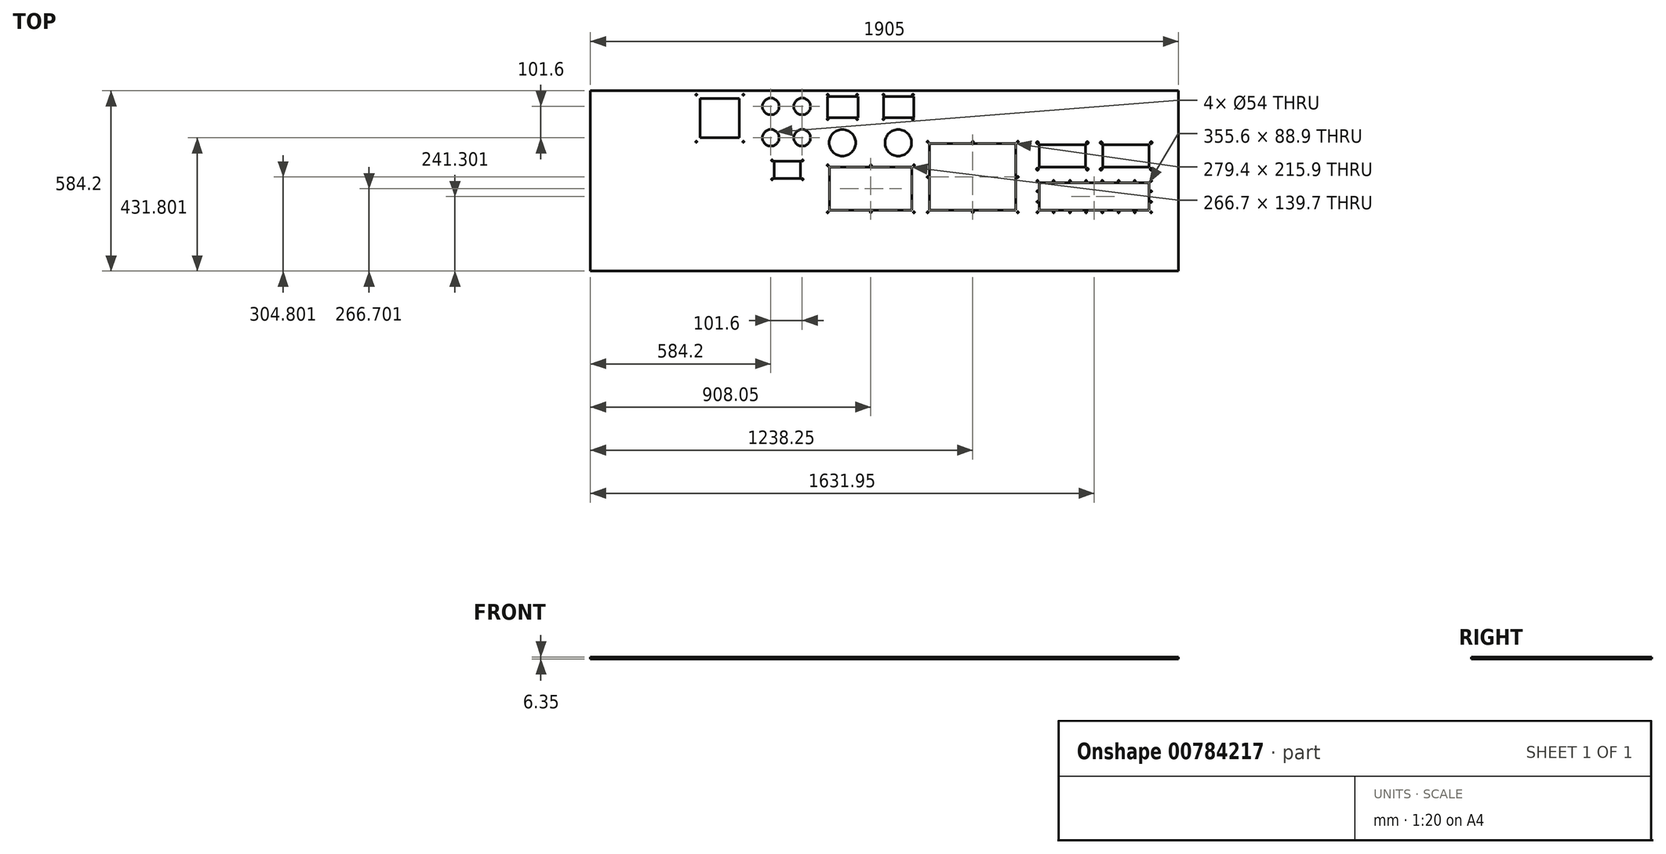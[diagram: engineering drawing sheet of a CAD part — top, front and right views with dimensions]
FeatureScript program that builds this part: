
annotation { "Feature Type Name" : "Feature", "Feature Type Description" : "" }
export const myFeature = defineFeature(function(context is Context, id is Id, definition is map)
    precondition{}
    {
        {
            var Q0;
            Q0=qCreatedBy(makeId("Top.planeOp"),FACE);
            var sketch = newSketch(context, id + "F0", { "sketchPlane" : qUnion([Q0])});
            skLineSegment(sketch, "E0.bottom", {"start": v(-452.65, 333.51) * mm, "end": v(1452.35, 333.51) * mm});
            skLineSegment(sketch, "E0.top", {"start": v(-452.65, -250.69) * mm, "end": v(1452.35, -250.69) * mm});
            skLineSegment(sketch, "E0.left", {"start": v(-452.65, 333.51) * mm, "end": v(-452.65, -250.69) * mm});
            skLineSegment(sketch, "E0.right", {"start": v(1452.35, 333.51) * mm, "end": v(1452.35, -250.69) * mm});
            skPoint(sketch, "E1", {"position": v(995.15, 41.41) * mm});
            skPoint(sketch, "E2", {"position": v(1363.45, 41.41) * mm});
            skPoint(sketch, "E3", {"position": v(1363.45, -60.19) * mm});
            skPoint(sketch, "E4", {"position": v(995.15, -60.19) * mm});
            skLineSegment(sketch, "E5", {"start": v(995.15, 41.41) * mm, "end": v(995.15, -60.19) * mm});
            skPoint(sketch, "E6", {"position": v(995.15, 7.63) * mm});
            skPoint(sketch, "E7", {"position": v(995.15, -26.15) * mm});
            skLineSegment(sketch, "E8", {"start": v(995.15, 41.41) * mm, "end": v(1363.45, 41.41) * mm});
            skLineSegment(sketch, "E9", {"start": v(1363.45, 41.41) * mm, "end": v(1363.45, -60.19) * mm});
            skLineSegment(sketch, "E10", {"start": v(1363.45, -60.19) * mm, "end": v(995.15, -60.19) * mm});
            skPoint(sketch, "E11", {"position": v(1047.73, 41.41) * mm});
            skPoint(sketch, "E12", {"position": v(1100.3, 41.41) * mm});
            skPoint(sketch, "E13", {"position": v(1152.88, 41.41) * mm});
            skPoint(sketch, "E14", {"position": v(1205.46, 41.41) * mm});
            skPoint(sketch, "E15", {"position": v(1258.04, 41.41) * mm});
            skPoint(sketch, "E16", {"position": v(1310.62, 41.41) * mm});
            skPoint(sketch, "E17", {"position": v(1047.73, -60.19) * mm});
            skPoint(sketch, "E18", {"position": v(1100.3, -60.19) * mm});
            skPoint(sketch, "E19", {"position": v(1152.88, -60.19) * mm});
            skPoint(sketch, "E20", {"position": v(1205.46, -60.19) * mm});
            skPoint(sketch, "E21", {"position": v(1258.04, -60.19) * mm});
            skPoint(sketch, "E22", {"position": v(1310.62, -60.19) * mm});
            skPoint(sketch, "E23", {"position": v(1363.45, 7.63) * mm});
            skPoint(sketch, "E24", {"position": v(1363.45, -26.4) * mm});
            skLineSegment(sketch, "E25.bottom", {"start": v(1001.5, 35.06) * mm, "end": v(1357.1, 35.06) * mm});
            skLineSegment(sketch, "E25.top", {"start": v(1001.5, -53.84) * mm, "end": v(1357.1, -53.84) * mm});
            skLineSegment(sketch, "E25.left", {"start": v(1001.5, 35.06) * mm, "end": v(1001.5, -53.84) * mm});
            skLineSegment(sketch, "E25.right", {"start": v(1357.1, 35.06) * mm, "end": v(1357.1, -53.84) * mm});
            skPoint(sketch, "E26", {"position": v(639.55, 168.41) * mm});
            skPoint(sketch, "E27", {"position": v(931.65, 168.41) * mm});
            skPoint(sketch, "E28", {"position": v(931.65, -60.19) * mm});
            skPoint(sketch, "E29", {"position": v(639.55, -60.19) * mm});
            skPoint(sketch, "E30", {"position": v(785.6, 168.41) * mm});
            skPoint(sketch, "E31", {"position": v(785.6, -60.19) * mm});
            skPoint(sketch, "E32", {"position": v(639.55, 54.11) * mm});
            skPoint(sketch, "E33", {"position": v(931.65, 54.11) * mm});
            skLineSegment(sketch, "E34", {"start": v(639.55, 168.41) * mm, "end": v(639.55, 54.11) * mm});
            skLineSegment(sketch, "E35", {"start": v(639.55, -60.19) * mm, "end": v(639.55, 54.11) * mm});
            skLineSegment(sketch, "E36", {"start": v(639.55, -60.19) * mm, "end": v(785.6, -60.19) * mm});
            skLineSegment(sketch, "E37", {"start": v(931.65, -60.19) * mm, "end": v(785.6, -60.19) * mm});
            skLineSegment(sketch, "E38", {"start": v(931.65, -60.19) * mm, "end": v(931.65, 168.41) * mm});
            skLineSegment(sketch, "E39", {"start": v(931.65, 168.41) * mm, "end": v(639.55, 168.41) * mm});
            skLineSegment(sketch, "E40.bottom", {"start": v(645.9, 162.06) * mm, "end": v(925.3, 162.06) * mm});
            skLineSegment(sketch, "E40.top", {"start": v(645.9, -53.84) * mm, "end": v(925.3, -53.84) * mm});
            skLineSegment(sketch, "E40.left", {"start": v(645.9, 162.06) * mm, "end": v(645.9, -53.84) * mm});
            skLineSegment(sketch, "E40.right", {"start": v(925.3, 162.06) * mm, "end": v(925.3, -53.84) * mm});
            skPoint(sketch, "E41", {"position": v(315.7, 92.21) * mm});
            skPoint(sketch, "E42", {"position": v(315.7, -60.19) * mm});
            skPoint(sketch, "E43", {"position": v(595.1, -60.19) * mm});
            skPoint(sketch, "E44", {"position": v(595.1, 92.21) * mm});
            skPoint(sketch, "E45", {"position": v(455.4, 92.21) * mm});
            skPoint(sketch, "E46", {"position": v(455.4, -60.19) * mm});
            skLineSegment(sketch, "E47", {"start": v(315.7, 92.21) * mm, "end": v(595.1, 92.21) * mm});
            skLineSegment(sketch, "E48", {"start": v(595.1, -60.19) * mm, "end": v(595.1, 92.21) * mm});
            skLineSegment(sketch, "E49", {"start": v(595.1, -60.19) * mm, "end": v(315.7, -60.19) * mm});
            skLineSegment(sketch, "E50", {"start": v(315.7, -60.19) * mm, "end": v(315.7, 92.21) * mm});
            skLineSegment(sketch, "E51.bottom", {"start": v(322.05, 85.86) * mm, "end": v(588.75, 85.86) * mm});
            skLineSegment(sketch, "E51.top", {"start": v(322.05, -53.84) * mm, "end": v(588.75, -53.84) * mm});
            skLineSegment(sketch, "E51.left", {"start": v(322.05, 85.86) * mm, "end": v(322.05, -53.84) * mm});
            skLineSegment(sketch, "E51.right", {"start": v(588.75, 85.86) * mm, "end": v(588.75, -53.84) * mm});
            skPoint(sketch, "E52", {"position": v(995.15, 165.11) * mm});
            skPoint(sketch, "E53", {"position": v(995.15, 79.51) * mm});
            skPoint(sketch, "E54", {"position": v(1156.95, 79.51) * mm});
            skPoint(sketch, "E55", {"position": v(1156.95, 165.11) * mm});
            skLineSegment(sketch, "E56", {"start": v(995.15, 165.11) * mm, "end": v(995.15, 79.51) * mm});
            skLineSegment(sketch, "E57", {"start": v(995.15, 79.51) * mm, "end": v(1156.95, 79.51) * mm});
            skLineSegment(sketch, "E58", {"start": v(1156.95, 79.51) * mm, "end": v(1156.95, 165.11) * mm});
            skLineSegment(sketch, "E59", {"start": v(1156.95, 165.11) * mm, "end": v(995.15, 165.11) * mm});
            skLineSegment(sketch, "E60.bottom", {"start": v(1001.5, 158.76) * mm, "end": v(1150.6, 158.76) * mm});
            skLineSegment(sketch, "E60.top", {"start": v(1001.5, 85.86) * mm, "end": v(1150.6, 85.86) * mm});
            skLineSegment(sketch, "E60.left", {"start": v(1001.5, 158.76) * mm, "end": v(1001.5, 85.86) * mm});
            skLineSegment(sketch, "E60.right", {"start": v(1150.6, 158.76) * mm, "end": v(1150.6, 85.86) * mm});
            skPoint(sketch, "E61", {"position": v(1201.65, 165.11) * mm});
            skPoint(sketch, "E62", {"position": v(1201.65, 79.51) * mm});
            skPoint(sketch, "E63", {"position": v(1363.45, 79.51) * mm});
            skPoint(sketch, "E64", {"position": v(1363.45, 165.11) * mm});
            skLineSegment(sketch, "E65", {"start": v(1201.65, 165.11) * mm, "end": v(1201.65, 79.51) * mm});
            skLineSegment(sketch, "E66", {"start": v(1201.65, 79.51) * mm, "end": v(1363.45, 79.51) * mm});
            skLineSegment(sketch, "E67", {"start": v(1363.45, 79.51) * mm, "end": v(1363.45, 165.11) * mm});
            skLineSegment(sketch, "E68", {"start": v(1363.45, 165.11) * mm, "end": v(1201.65, 165.11) * mm});
            skLineSegment(sketch, "E69.bottom", {"start": v(1206.48, 158.76) * mm, "end": v(1357.1, 158.76) * mm});
            skLineSegment(sketch, "E69.top", {"start": v(1206.48, 85.86) * mm, "end": v(1357.1, 85.86) * mm});
            skLineSegment(sketch, "E69.left", {"start": v(1206.48, 158.76) * mm, "end": v(1206.48, 85.86) * mm});
            skLineSegment(sketch, "E69.right", {"start": v(1357.1, 158.76) * mm, "end": v(1357.1, 85.86) * mm});
            skPoint(sketch, "E70", {"position": v(315.7, 320.81) * mm});
            skPoint(sketch, "E71", {"position": v(315.7, 241.34) * mm});
            skPoint(sketch, "E72", {"position": v(411.18, 241.34) * mm});
            skPoint(sketch, "E73", {"position": v(411.18, 320.81) * mm});
            skLineSegment(sketch, "E74", {"start": v(315.7, 320.81) * mm, "end": v(411.18, 320.81) * mm});
            skLineSegment(sketch, "E75", {"start": v(411.18, 241.34) * mm, "end": v(411.18, 320.81) * mm});
            skLineSegment(sketch, "E76", {"start": v(411.18, 241.34) * mm, "end": v(315.7, 241.34) * mm});
            skLineSegment(sketch, "E77", {"start": v(315.7, 241.34) * mm, "end": v(315.7, 320.81) * mm});
            skLineSegment(sketch, "E78.bottom", {"start": v(315.7, 314.46) * mm, "end": v(414.13, 314.46) * mm});
            skLineSegment(sketch, "E78.top", {"start": v(315.7, 246.2) * mm, "end": v(414.13, 246.2) * mm});
            skLineSegment(sketch, "E78.left", {"start": v(315.7, 314.46) * mm, "end": v(315.7, 246.2) * mm});
            skLineSegment(sketch, "E78.right", {"start": v(414.13, 314.46) * mm, "end": v(414.13, 246.2) * mm});
            skPoint(sketch, "E79", {"position": v(496.68, 320.81) * mm});
            skPoint(sketch, "E80", {"position": v(496.68, 241.34) * mm});
            skPoint(sketch, "E81", {"position": v(592.15, 241.34) * mm});
            skPoint(sketch, "E82", {"position": v(592.15, 320.81) * mm});
            skLineSegment(sketch, "E83", {"start": v(496.68, 320.81) * mm, "end": v(592.15, 320.81) * mm});
            skLineSegment(sketch, "E84", {"start": v(592.15, 241.34) * mm, "end": v(592.15, 320.81) * mm});
            skLineSegment(sketch, "E85", {"start": v(592.15, 241.34) * mm, "end": v(496.68, 241.34) * mm});
            skLineSegment(sketch, "E86", {"start": v(496.68, 241.34) * mm, "end": v(496.68, 320.81) * mm});
            skLineSegment(sketch, "E87.bottom", {"start": v(496.68, 314.46) * mm, "end": v(595.1, 314.46) * mm});
            skLineSegment(sketch, "E87.top", {"start": v(496.68, 246.2) * mm, "end": v(595.1, 246.2) * mm});
            skLineSegment(sketch, "E87.left", {"start": v(496.68, 314.46) * mm, "end": v(496.68, 246.2) * mm});
            skLineSegment(sketch, "E87.right", {"start": v(595.1, 314.46) * mm, "end": v(595.1, 246.2) * mm});
            skPoint(sketch, "E88", {"position": v(233.15, 282.71) * mm});
            skPoint(sketch, "E89", {"position": v(233.15, 181.11) * mm});
            skPoint(sketch, "E90", {"position": v(131.55, 282.71) * mm});
            skPoint(sketch, "E91", {"position": v(131.55, 181.11) * mm});
            skPoint(sketch, "E92", {"position": v(363.44, 165.14) * mm});
            skPoint(sketch, "E92.positionSnap0", {"position": v(363.44, 241.34) * mm});
            skPoint(sketch, "E93", {"position": v(544.41, 165.14) * mm});
            skPoint(sketch, "E93.positionSnap0", {"position": v(544.41, 241.34) * mm});
            skPoint(sketch, "E94", {"position": v(135.61, 107.93) * mm});
            skPoint(sketch, "E95", {"position": v(234.61, 107.93) * mm});
            skPoint(sketch, "E96", {"position": v(234.61, 46.72) * mm});
            skPoint(sketch, "E97", {"position": v(135.61, 46.72) * mm});
            skLineSegment(sketch, "E98.bottom", {"start": v(143.03, 104.91) * mm, "end": v(227.2, 104.91) * mm});
            skLineSegment(sketch, "E98.top", {"start": v(143.03, 49.75) * mm, "end": v(227.2, 49.75) * mm});
            skLineSegment(sketch, "E98.left", {"start": v(143.03, 104.91) * mm, "end": v(143.03, 49.75) * mm});
            skLineSegment(sketch, "E98.right", {"start": v(227.2, 104.91) * mm, "end": v(227.2, 49.75) * mm});
            skLineSegment(sketch, "E99", {"start": v(131.55, 181.11) * mm, "end": v(233.15, 181.11) * mm});
            skPoint(sketch, "E100", {"position": v(-109.75, 320.81) * mm});
            skPoint(sketch, "E101", {"position": v(42.65, 320.81) * mm});
            skPoint(sketch, "E102", {"position": v(42.65, 168.41) * mm});
            skPoint(sketch, "E103", {"position": v(-109.75, 168.41) * mm});
            skLineSegment(sketch, "E104.bottom", {"start": v(-97.05, 308.11) * mm, "end": v(29.95, 308.11) * mm});
            skLineSegment(sketch, "E104.top", {"start": v(-97.05, 181.11) * mm, "end": v(29.95, 181.11) * mm});
            skLineSegment(sketch, "E104.left", {"start": v(-97.05, 308.11) * mm, "end": v(-97.05, 181.11) * mm});
            skLineSegment(sketch, "E104.right", {"start": v(29.95, 308.11) * mm, "end": v(29.95, 181.11) * mm});
            skSolve(sketch);
        }
        {
            var Q0;
            Q0=makeQuery(id+"F0.imprint","IMPRINT",FACE,{"disambiguationData":[TD([[makeQuery(id+"F0.imprint","IMPRINT",EDGE,{"derivedFrom":sQuery(id+"F0.wireOp",EDGE,"E0.bottom")}),-1.0]])]});
            var Q1;
            Q1=makeQuery(id+"F0.imprint","IMPRINT",FACE,{"disambiguationData":[TD([[makeQuery(id+"F0.imprint","IMPRINT",EDGE,{"derivedFrom":sQuery(id+"F0.wireOp",EDGE,"E5")}),1.0]])]});
            var Q2;
            Q2=makeQuery(id+"F0.imprint","IMPRINT",FACE,{"disambiguationData":[TD([[makeQuery(id+"F0.imprint","IMPRINT",EDGE,{"derivedFrom":sQuery(id+"F0.wireOp",EDGE,"E34")}),1.0]])]});
            var Q3;
            Q3=makeQuery(id+"F0.imprint","IMPRINT",FACE,{"disambiguationData":[TD([[makeQuery(id+"F0.imprint","IMPRINT",EDGE,{"derivedFrom":sQuery(id+"F0.wireOp",EDGE,"E47")}),-1.0]])]});
            var Q4;
            Q4=makeQuery(id+"F0.imprint","IMPRINT",FACE,{"disambiguationData":[TD([[makeQuery(id+"F0.imprint","IMPRINT",EDGE,{"derivedFrom":sQuery(id+"F0.wireOp",EDGE,"E56")}),1.0]])]});
            var Q5;
            Q5=makeQuery(id+"F0.imprint","IMPRINT",FACE,{"disambiguationData":[TD([[makeQuery(id+"F0.imprint","IMPRINT",EDGE,{"derivedFrom":sQuery(id+"F0.wireOp",EDGE,"E65")}),1.0]])]});
            var Q6;
            {var subQ0=sQuery(id+"F0.wireOp",EDGE,"E74");Q6=makeQuery(id+"F0.imprint","IMPRINT",FACE,{"disambiguationData":[TD([[makeQuery(id+"F0.imprint","IMPRINT",EDGE,{"derivedFrom":subQ0}),-1.0]])]});}
            var Q7;
            {var subQ0=sQuery(id+"F0.wireOp",EDGE,"E76");Q7=makeQuery(id+"F0.imprint","IMPRINT",FACE,{"disambiguationData":[TD([[makeQuery(id+"F0.imprint","IMPRINT",EDGE,{"derivedFrom":subQ0}),-1.0]])]});}
            var Q8;
            {var subQ0=sQuery(id+"F0.wireOp",EDGE,"E83");Q8=makeQuery(id+"F0.imprint","IMPRINT",FACE,{"disambiguationData":[TD([[makeQuery(id+"F0.imprint","IMPRINT",EDGE,{"derivedFrom":subQ0}),-1.0]])]});}
            var Q9;
            {var subQ0=sQuery(id+"F0.wireOp",EDGE,"E85");Q9=makeQuery(id+"F0.imprint","IMPRINT",FACE,{"disambiguationData":[TD([[makeQuery(id+"F0.imprint","IMPRINT",EDGE,{"derivedFrom":subQ0}),-1.0]])]});}
            extrude(context, id + "F1", {"entities" : qUnion([Q0, Q1, Q2, Q3, Q4, Q5, Q6, Q7, Q8, Q9]), "depth" : 6.35 * mm, "offsetDistance" : 25.4 * mm});
        }
        {
            var Q0;
            Q0=sQuery(id+"F0.wireOp",VERTEX,"c7c97ea6-c91f-4cfa-ac0e-7772fff2237e");
            var Q1;
            Q1=sQuery(id+"F0.wireOp",VERTEX,"E5.start");
            var Q2;
            Q2=sQuery(id+"F0.wireOp",VERTEX,"E6");
            var Q3;
            Q3=sQuery(id+"F0.wireOp",VERTEX,"E7");
            var Q4;
            Q4=sQuery(id+"F0.wireOp",VERTEX,"E4");
            var Q5;
            Q5=sQuery(id+"F0.wireOp",VERTEX,"E17");
            var Q6;
            Q6=sQuery(id+"F0.wireOp",VERTEX,"E18");
            var Q7;
            Q7=sQuery(id+"F0.wireOp",VERTEX,"E19");
            var Q8;
            Q8=sQuery(id+"F0.wireOp",VERTEX,"E20");
            var Q9;
            Q9=sQuery(id+"F0.wireOp",VERTEX,"E21");
            var Q10;
            Q10=sQuery(id+"F0.wireOp",VERTEX,"E22");
            var Q11;
            Q11=sQuery(id+"F0.wireOp",VERTEX,"E3");
            var Q12;
            Q12=sQuery(id+"F0.wireOp",VERTEX,"E24");
            var Q13;
            Q13=sQuery(id+"F0.wireOp",VERTEX,"E23");
            var Q14;
            Q14=sQuery(id+"F0.wireOp",VERTEX,"E2");
            var Q15;
            Q15=sQuery(id+"F0.wireOp",VERTEX,"E16");
            var Q16;
            Q16=sQuery(id+"F0.wireOp",VERTEX,"E15");
            var Q17;
            Q17=sQuery(id+"F0.wireOp",VERTEX,"E14");
            var Q18;
            Q18=sQuery(id+"F0.wireOp",VERTEX,"E13");
            var Q19;
            Q19=sQuery(id+"F0.wireOp",VERTEX,"E12");
            var Q20;
            Q20=sQuery(id+"F0.wireOp",VERTEX,"E11");
            var Q21;
            Q21=sQuery(id+"F0.wireOp",VERTEX,"E26");
            var Q22;
            Q22=sQuery(id+"F0.wireOp",VERTEX,"E30");
            var Q23;
            Q23=sQuery(id+"F0.wireOp",VERTEX,"E27");
            var Q24;
            Q24=sQuery(id+"F0.wireOp",VERTEX,"E33");
            var Q25;
            Q25=sQuery(id+"F0.wireOp",VERTEX,"E28");
            var Q26;
            Q26=sQuery(id+"F0.wireOp",VERTEX,"E31");
            var Q27;
            Q27=sQuery(id+"F0.wireOp",VERTEX,"E29");
            var Q28;
            Q28=sQuery(id+"F0.wireOp",VERTEX,"E32");
            var Q29;
            Q29=sQuery(id+"F0.wireOp",VERTEX,"E41");
            var Q30;
            Q30=sQuery(id+"F0.wireOp",VERTEX,"E45");
            var Q31;
            Q31=sQuery(id+"F0.wireOp",VERTEX,"E44");
            var Q32;
            Q32=sQuery(id+"F0.wireOp",VERTEX,"E43");
            var Q33;
            Q33=sQuery(id+"F0.wireOp",VERTEX,"E46");
            var Q34;
            Q34=sQuery(id+"F0.wireOp",VERTEX,"E42");
            var Q35;
            Q35=sQuery(id+"F0.wireOp",VERTEX,"E70");
            var Q36;
            Q36=sQuery(id+"F0.wireOp",VERTEX,"E73");
            var Q37;
            Q37=sQuery(id+"F0.wireOp",VERTEX,"E72");
            var Q38;
            Q38=sQuery(id+"F0.wireOp",VERTEX,"E71");
            var Q39;
            Q39=sQuery(id+"F0.wireOp",VERTEX,"E79");
            var Q40;
            Q40=sQuery(id+"F0.wireOp",VERTEX,"E80");
            var Q41;
            Q41=sQuery(id+"F0.wireOp",VERTEX,"E81");
            var Q42;
            Q42=sQuery(id+"F0.wireOp",VERTEX,"E82");
            var Q43;
            Q43=sQuery(id+"F0.wireOp",VERTEX,"E94");
            var Q44;
            Q44=sQuery(id+"F0.wireOp",VERTEX,"E95");
            var Q45;
            Q45=sQuery(id+"F0.wireOp",VERTEX,"E96");
            var Q46;
            Q46=sQuery(id+"F0.wireOp",VERTEX,"E97");
            var Q47;
            Q47=sQuery(id+"F0.wireOp",VERTEX,"E100");
            var Q48;
            Q48=sQuery(id+"F0.wireOp",VERTEX,"E103");
            var Q49;
            Q49=sQuery(id+"F0.wireOp",VERTEX,"E102");
            var Q50;
            Q50=sQuery(id+"F0.wireOp",VERTEX,"E101");
            var Q51;
            Q51=makeQuery(id+"F1.opExtrude","SWEPT_BODY",BODY,{"disambiguationData":[OSD([sQuery(id+"F0.wireOp",EDGE,"E0.bottom"),sQuery(id+"F0.wireOp",EDGE,"E0.top"),sQuery(id+"F0.wireOp",EDGE,"E0.left"),sQuery(id+"F0.wireOp",EDGE,"E0.right")])]});
            hole(context, id + "F2", {"style" : HoleStyle.SIMPLE, "endStyle" : HoleEndStyle.THROUGH, "oppositeDirection" : true, "holeDiameter" : 4.17 * mm, "majorDiameter" : 6.35 * mm, "isTappedThrough" : true, "tappedDepth" : 12.7 * mm, "tapClearance" : 3, "locations" : qUnion([Q0, Q1, Q2, Q3, Q4, Q5, Q6, Q7, Q8, Q9, Q10, Q11, Q12, Q13, Q14, Q15, Q16, Q17, Q18, Q19, Q20, Q21, Q22, Q23, Q24, Q25, Q26, Q27, Q28, Q29, Q30, Q31, Q32, Q33, Q34, Q35, Q36, Q37, Q38, Q39, Q40, Q41, Q42, Q43, Q44, Q45, Q46, Q47, Q48, Q49, Q50]), "scope" : qUnion([Q51])});
        }
        {
            var Q0;
            Q0=sQuery(id+"F0.wireOp",VERTEX,"E52");
            var Q1;
            Q1=sQuery(id+"F0.wireOp",VERTEX,"E53");
            var Q2;
            Q2=sQuery(id+"F0.wireOp",VERTEX,"E54");
            var Q3;
            Q3=sQuery(id+"F0.wireOp",VERTEX,"E55");
            var Q4;
            Q4=sQuery(id+"F0.wireOp",VERTEX,"E61");
            var Q5;
            Q5=sQuery(id+"F0.wireOp",VERTEX,"E62");
            var Q6;
            Q6=sQuery(id+"F0.wireOp",VERTEX,"E63");
            var Q7;
            Q7=sQuery(id+"F0.wireOp",VERTEX,"E64");
            var Q8;
            Q8=makeQuery(id+"F1.opExtrude","SWEPT_BODY",BODY,{"disambiguationData":[OSD([sQuery(id+"F0.wireOp",EDGE,"E0.bottom"),sQuery(id+"F0.wireOp",EDGE,"E0.top"),sQuery(id+"F0.wireOp",EDGE,"E0.left"),sQuery(id+"F0.wireOp",EDGE,"E0.right"),sQuery(id+"F0.wireOp",EDGE,"E25.bottom"),sQuery(id+"F0.wireOp",EDGE,"E25.top"),sQuery(id+"F0.wireOp",EDGE,"E25.left"),sQuery(id+"F0.wireOp",EDGE,"E25.right"),sQuery(id+"F0.wireOp",EDGE,"E40.bottom"),sQuery(id+"F0.wireOp",EDGE,"E40.top"),sQuery(id+"F0.wireOp",EDGE,"E40.left"),sQuery(id+"F0.wireOp",EDGE,"E40.right"),sQuery(id+"F0.wireOp",EDGE,"E51.bottom"),sQuery(id+"F0.wireOp",EDGE,"E51.top"),sQuery(id+"F0.wireOp",EDGE,"E51.left"),sQuery(id+"F0.wireOp",EDGE,"E51.right"),sQuery(id+"F0.wireOp",EDGE,"E60.bottom"),sQuery(id+"F0.wireOp",EDGE,"E60.top"),sQuery(id+"F0.wireOp",EDGE,"E60.left"),sQuery(id+"F0.wireOp",EDGE,"E60.right")])]});
            hole(context, id + "F3", {"style" : HoleStyle.SIMPLE, "endStyle" : HoleEndStyle.THROUGH, "oppositeDirection" : true, "holeDiameter" : 7 * mm, "majorDiameter" : 6.35 * mm, "isTappedThrough" : true, "tappedDepth" : 12.7 * mm, "tapClearance" : 3, "locations" : qUnion([Q0, Q1, Q2, Q3, Q4, Q5, Q6, Q7]), "scope" : qUnion([Q8])});
        }
        {
            var Q0;
            Q0=sQuery(id+"F0.wireOp",VERTEX,"E89");
            var Q1;
            Q1=sQuery(id+"F0.wireOp",VERTEX,"E88");
            var Q2;
            Q2=sQuery(id+"F0.wireOp",VERTEX,"E91");
            var Q3;
            Q3=sQuery(id+"F0.wireOp",VERTEX,"E90");
            var Q4;
            Q4=makeQuery(id+"F1.opExtrude","SWEPT_BODY",BODY,{"disambiguationData":[OSD([sQuery(id+"F0.wireOp",EDGE,"E0.bottom"),sQuery(id+"F0.wireOp",EDGE,"E0.top"),sQuery(id+"F0.wireOp",EDGE,"E0.left"),sQuery(id+"F0.wireOp",EDGE,"E0.right"),sQuery(id+"F0.wireOp",EDGE,"E25.bottom"),sQuery(id+"F0.wireOp",EDGE,"E25.top"),sQuery(id+"F0.wireOp",EDGE,"E25.left"),sQuery(id+"F0.wireOp",EDGE,"E25.right"),sQuery(id+"F0.wireOp",EDGE,"E40.bottom"),sQuery(id+"F0.wireOp",EDGE,"E40.top"),sQuery(id+"F0.wireOp",EDGE,"E40.left"),sQuery(id+"F0.wireOp",EDGE,"E40.right"),sQuery(id+"F0.wireOp",EDGE,"E51.bottom"),sQuery(id+"F0.wireOp",EDGE,"E51.top"),sQuery(id+"F0.wireOp",EDGE,"E51.left"),sQuery(id+"F0.wireOp",EDGE,"E51.right"),sQuery(id+"F0.wireOp",EDGE,"E60.bottom"),sQuery(id+"F0.wireOp",EDGE,"E60.top"),sQuery(id+"F0.wireOp",EDGE,"E60.left"),sQuery(id+"F0.wireOp",EDGE,"E60.right"),sQuery(id+"F0.wireOp",EDGE,"E69.bottom"),sQuery(id+"F0.wireOp",EDGE,"E69.top"),sQuery(id+"F0.wireOp",EDGE,"E69.left"),sQuery(id+"F0.wireOp",EDGE,"E69.right"),sQuery(id+"F0.wireOp",EDGE,"E78.bottom"),sQuery(id+"F0.wireOp",EDGE,"E78.top"),sQuery(id+"F0.wireOp",EDGE,"E78.left"),sQuery(id+"F0.wireOp",EDGE,"E78.right"),sQuery(id+"F0.wireOp",EDGE,"E87.bottom"),sQuery(id+"F0.wireOp",EDGE,"E87.top"),sQuery(id+"F0.wireOp",EDGE,"E87.left"),sQuery(id+"F0.wireOp",EDGE,"E87.right")])]});
            hole(context, id + "F4", {"style" : HoleStyle.SIMPLE, "endStyle" : HoleEndStyle.THROUGH, "oppositeDirection" : true, "holeDiameter" : 54 * mm, "majorDiameter" : 6.35 * mm, "isTappedThrough" : true, "tappedDepth" : 12.7 * mm, "tapClearance" : 3, "locations" : qUnion([Q0, Q1, Q2, Q3]), "scope" : qUnion([Q4])});
        }
        {
            var Q0;
            Q0=sQuery(id+"F0.wireOp",VERTEX,"E92");
            var Q1;
            Q1=sQuery(id+"F0.wireOp",VERTEX,"E93");
            var Q2;
            Q2=makeQuery(id+"F1.opExtrude","SWEPT_BODY",BODY,{"disambiguationData":[OSD([sQuery(id+"F0.wireOp",EDGE,"E0.bottom"),sQuery(id+"F0.wireOp",EDGE,"E0.top"),sQuery(id+"F0.wireOp",EDGE,"E0.left"),sQuery(id+"F0.wireOp",EDGE,"E0.right"),sQuery(id+"F0.wireOp",EDGE,"E25.bottom"),sQuery(id+"F0.wireOp",EDGE,"E25.top"),sQuery(id+"F0.wireOp",EDGE,"E25.left"),sQuery(id+"F0.wireOp",EDGE,"E25.right"),sQuery(id+"F0.wireOp",EDGE,"E40.bottom"),sQuery(id+"F0.wireOp",EDGE,"E40.top"),sQuery(id+"F0.wireOp",EDGE,"E40.left"),sQuery(id+"F0.wireOp",EDGE,"E40.right"),sQuery(id+"F0.wireOp",EDGE,"E51.bottom"),sQuery(id+"F0.wireOp",EDGE,"E51.top"),sQuery(id+"F0.wireOp",EDGE,"E51.left"),sQuery(id+"F0.wireOp",EDGE,"E51.right"),sQuery(id+"F0.wireOp",EDGE,"E60.bottom"),sQuery(id+"F0.wireOp",EDGE,"E60.top"),sQuery(id+"F0.wireOp",EDGE,"E60.left"),sQuery(id+"F0.wireOp",EDGE,"E60.right"),sQuery(id+"F0.wireOp",EDGE,"E69.bottom"),sQuery(id+"F0.wireOp",EDGE,"E69.top"),sQuery(id+"F0.wireOp",EDGE,"E69.left"),sQuery(id+"F0.wireOp",EDGE,"E69.right"),sQuery(id+"F0.wireOp",EDGE,"E78.bottom"),sQuery(id+"F0.wireOp",EDGE,"E78.top"),sQuery(id+"F0.wireOp",EDGE,"E78.left"),sQuery(id+"F0.wireOp",EDGE,"E78.right"),sQuery(id+"F0.wireOp",EDGE,"E87.bottom"),sQuery(id+"F0.wireOp",EDGE,"E87.top"),sQuery(id+"F0.wireOp",EDGE,"E87.left"),sQuery(id+"F0.wireOp",EDGE,"E87.right")])]});
            hole(context, id + "F5", {"style" : HoleStyle.SIMPLE, "endStyle" : HoleEndStyle.THROUGH, "oppositeDirection" : true, "holeDiameter" : 86 * mm, "majorDiameter" : 6.35 * mm, "isTappedThrough" : true, "tappedDepth" : 12.7 * mm, "tapClearance" : 3, "locations" : qUnion([Q0, Q1]), "scope" : qUnion([Q2])});
        }
    });
